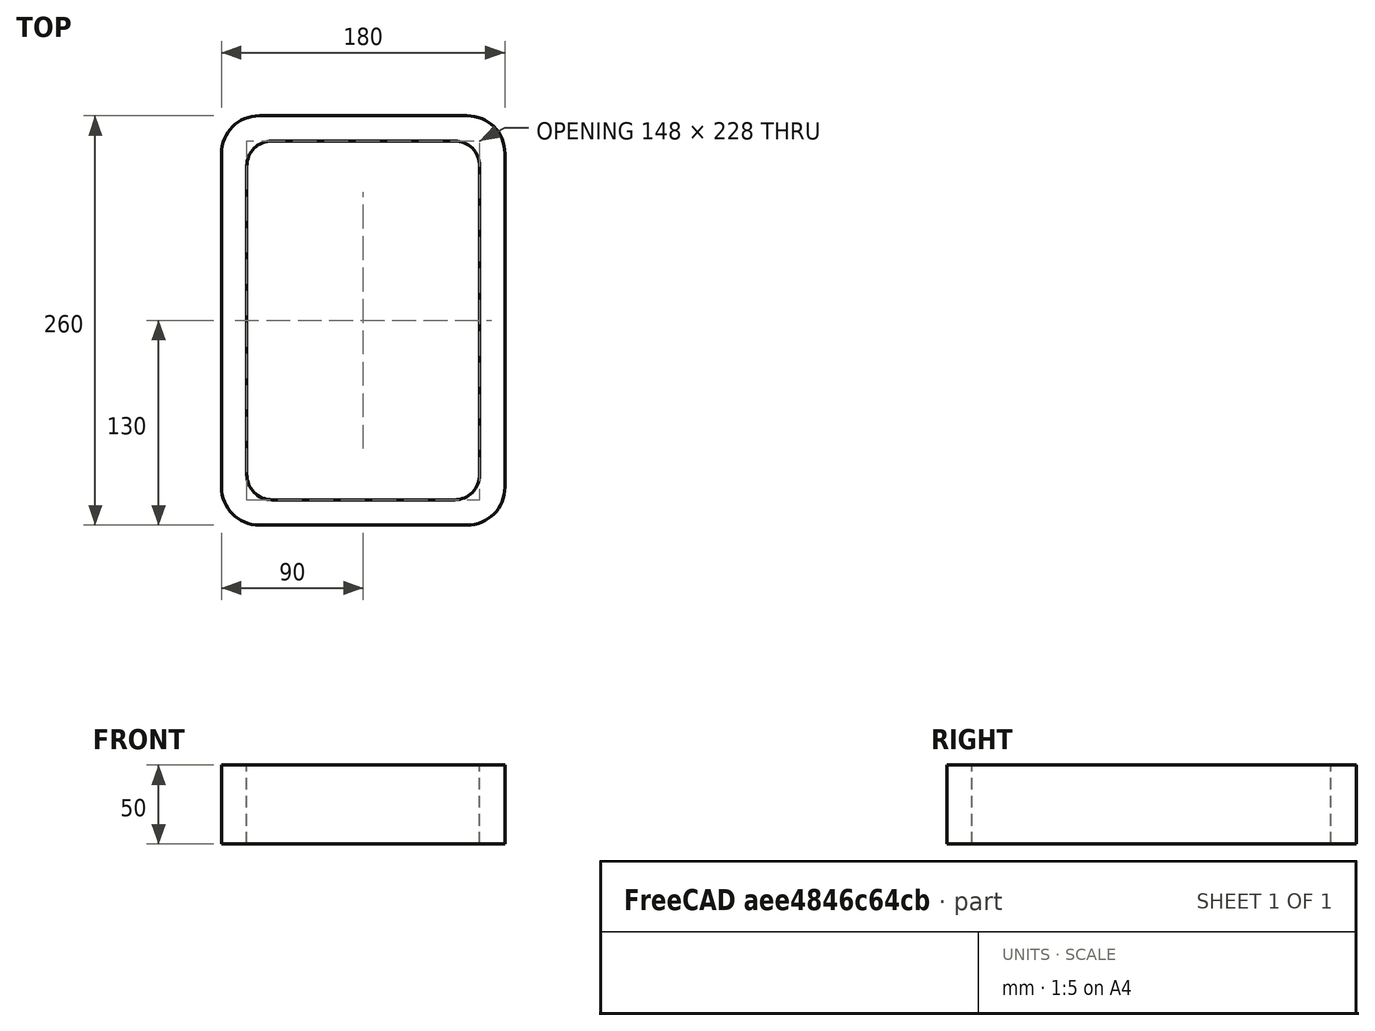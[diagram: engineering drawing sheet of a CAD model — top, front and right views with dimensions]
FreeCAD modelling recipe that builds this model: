
FCSTD DOCUMENT  (FreeCAD 0.15R4671 (Git))
Label: Rectangular hollow section 260x180x16 EN10219 S235JRH
License: All rights reserved
LicenseURL: http://en.wikipedia.org/wiki/All_rights_reserved
objects: Sketcher::SketchObject×1, Part::Extrusion×1
note: 2 computed .brp shape members not serialized (recipe doc carries the construction recipe); baked Part::Feature solids carry a one-line shape summary decoded from their .brp

FEATURE [Sketcher::SketchObject] Sketch
  sketch-geometry (16):
    g0: LineSegment StartX=-58 StartY=114 StartZ=0 EndX=58 EndY=114 EndZ=0
    g1: LineSegment StartX=74 StartY=98 StartZ=0 EndX=74 EndY=-98 EndZ=0
    g2: LineSegment StartX=58 StartY=-114 StartZ=0 EndX=-58 EndY=-114 EndZ=0
    g3: LineSegment StartX=-74 StartY=-98 StartZ=0 EndX=-74 EndY=98 EndZ=0
    g4: LineSegment StartX=-66 StartY=130 StartZ=0 EndX=66 EndY=130 EndZ=0
    g5: LineSegment StartX=90 StartY=106 StartZ=0 EndX=90 EndY=-106 EndZ=0
    g6: LineSegment StartX=66 StartY=-130 StartZ=0 EndX=-66 EndY=-130 EndZ=0
    g7: LineSegment StartX=-90 StartY=-106 StartZ=0 EndX=-90 EndY=106 EndZ=0
    g8: ArcOfCircle CenterX=-58 CenterY=98 CenterZ=0 NormalX=0 NormalY=0 NormalZ=1 Radius=16 StartAngle=1.5708 EndAngle=3.14159
    g9: ArcOfCircle CenterX=58 CenterY=98 CenterZ=0 NormalX=0 NormalY=0 NormalZ=1 Radius=16 StartAngle=0 EndAngle=1.5708
    g10: ArcOfCircle CenterX=58 CenterY=-98 CenterZ=0 NormalX=0 NormalY=0 NormalZ=1 Radius=16 StartAngle=4.71239 EndAngle=6.28319
    g11: ArcOfCircle CenterX=-58 CenterY=-98 CenterZ=0 NormalX=0 NormalY=0 NormalZ=1 Radius=16 StartAngle=3.14159 EndAngle=4.71239
    g12: ArcOfCircle CenterX=66 CenterY=106 CenterZ=0 NormalX=0 NormalY=0 NormalZ=1 Radius=24 StartAngle=0 EndAngle=1.5708
    g13: ArcOfCircle CenterX=66 CenterY=-106 CenterZ=0 NormalX=0 NormalY=0 NormalZ=1 Radius=24 StartAngle=4.71239 EndAngle=6.28319
    g14: ArcOfCircle CenterX=-66 CenterY=-106 CenterZ=0 NormalX=0 NormalY=0 NormalZ=1 Radius=24 StartAngle=3.14159 EndAngle=4.71239
    g15: ArcOfCircle CenterX=-66 CenterY=106 CenterZ=0 NormalX=0 NormalY=0 NormalZ=1 Radius=24 StartAngle=1.5708 EndAngle=3.14159
  constraints (36):
    c: Horizontal(g2)
    c: Vertical(g3)
    c: Horizontal(g6)
    c: Vertical(g7)
    c: Tangent(g3,g8) = 1.5708
    c: Tangent(g0,g8) = 1.5708
    c: Tangent(g0,g9) = 1.5708
    c: Tangent(g1,g9) = 1.5708
    c: Tangent(g1,g10) = 1.5708
    c: Tangent(g2,g10) = 1.5708
    c: Tangent(g2,g11) = 1.5708
    c: Tangent(g3,g11) = 1.5708
    c: Tangent(g4,g12) = 1.5708
    c: Tangent(g5,g12) = 1.5708
    c: Tangent(g5,g13) = 1.5708
    c: Tangent(g6,g13) = 1.5708
    c: Tangent(g6,g14) = 1.5708
    c: Tangent(g7,g14) = 1.5708
    c: Tangent(g7,g15) = 1.5708
    c: Tangent(g4,g15) = 1.5708
    c: Equal(g9,g8)
    c: Equal(g9,g11)
    c: Equal(g9,g10)
    c: Equal(g12,g15)
    c: Equal(g12,g14)
    c: Equal(g12,g13)
    c: Symmetric(g4,g6,g-1)
    c: Symmetric(g7,g5,g-2)
    c: DistanceY(g4,g6) = -260
    c: DistanceX(g7,g5) = 180
    c: Symmetric(g3,g1,g-2)
    c: Symmetric(g0,g2,g-1)
    c: DistanceY(g0,g4) = 16
    c: DistanceX(g5,g1) = -16
    c: Radius(g9) = 16
    c: Radius(g12) = 24
FEATURE [Part::Extrusion] Extrude  label="Rectangular hollow section 260x180x16 EN10219 S235JRH"
  Base = -> Sketch
  Dir = (0,0,50)
  Solid = true
